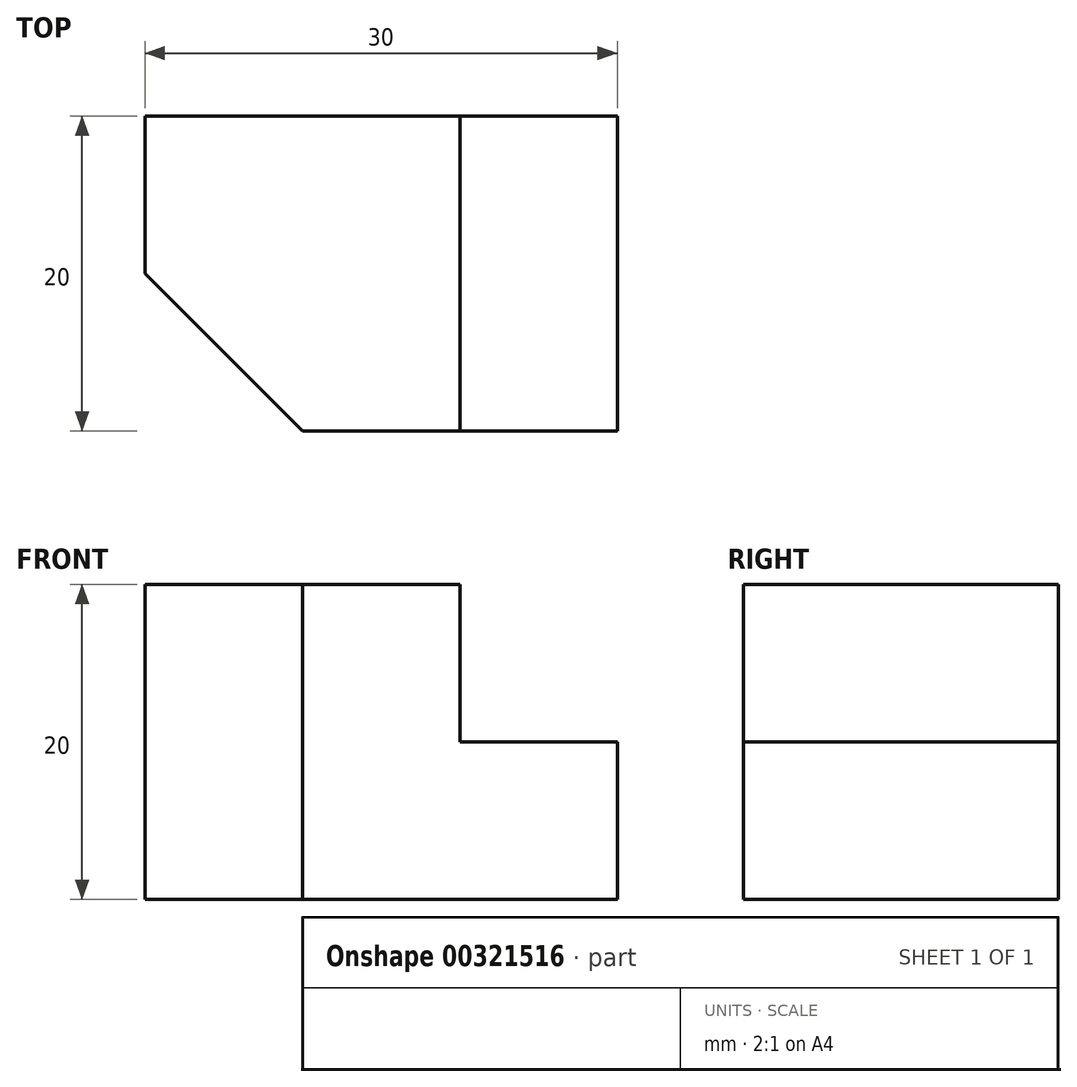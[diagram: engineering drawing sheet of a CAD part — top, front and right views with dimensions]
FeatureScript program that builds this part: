
annotation { "Feature Type Name" : "Feature", "Feature Type Description" : "" }
export const myFeature = defineFeature(function(context is Context, id is Id, definition is map)
    precondition{}
    {
        {
            var Q0;
            Q0=qCreatedBy(makeId("Front.planeOp"),FACE);
            var sketch = newSketch(context, id + "F0", { "sketchPlane" : qUnion([Q0])});
            skLineSegment(sketch, "E0.bottom", {"start": v(0, 0) * mm, "end": v(30, 0) * mm});
            skLineSegment(sketch, "E0.top", {"start": v(0, 20) * mm, "end": v(30, 20) * mm});
            skLineSegment(sketch, "E0.left", {"start": v(0, 0) * mm, "end": v(0, 20) * mm});
            skLineSegment(sketch, "E0.right", {"start": v(30, 0) * mm, "end": v(30, 20) * mm});
            skSolve(sketch);
        }
        {
            var Q0;
            Q0 = qSketchRegion(id + "F0", true);
            extrude(context, id + "F1", {"entities" : qUnion([Q0]), "depth" : (5 * 4) * mm});
        }
        {
            var Q0;
            Q0=makeQuery(id+"F1.opExtrude","CAP_FACE",FACE,{"disambiguationData":[OSD([sQuery(id+"F0.wireOp",EDGE,"E0.bottom"),sQuery(id+"F0.wireOp",EDGE,"E0.top"),sQuery(id+"F0.wireOp",EDGE,"E0.left"),sQuery(id+"F0.wireOp",EDGE,"E0.right")])],"isStart":false});
            var sketch = newSketch(context, id + "F2", { "sketchPlane" : qUnion([Q0])});
            skLineSegment(sketch, "E1.bottom", {"start": v(30, 20) * mm, "end": v(20, 20) * mm});
            skLineSegment(sketch, "E1.top", {"start": v(30, 10) * mm, "end": v(20, 10) * mm});
            skLineSegment(sketch, "E1.left", {"start": v(30, 20) * mm, "end": v(30, 10) * mm});
            skLineSegment(sketch, "E1.right", {"start": v(20, 20) * mm, "end": v(20, 10) * mm});
            skSolve(sketch);
        }
        {
            var Q0;
            Q0 = qSketchRegion(id + "F2", true);
            extrude(context, id + "F3", {"entities" : qUnion([Q0]), "operationType" : NewBodyOperationType.REMOVE, "endBound" : BoundingType.THROUGH_ALL, "oppositeDirection" : true, "depth" : 25 * mm});
        }
        {
            var Q0;
            Q0=makeQuery(id+"F1.opExtrude","SWEPT_FACE",FACE,{"disambiguationData":[OSD([sQuery(id+"F0.wireOp",EDGE,"E0.top")])]});
            var sketch = newSketch(context, id + "F4", { "sketchPlane" : qUnion([Q0])});
            skLineSegment(sketch, "E2", {"start": v(0, -20) * mm, "end": v(0, -10) * mm});
            skLineSegment(sketch, "E3", {"start": v(0, -20) * mm, "end": v(10, -20) * mm});
            skLineSegment(sketch, "E4", {"start": v(10, -20) * mm, "end": v(0, -10) * mm});
            skSolve(sketch);
        }
        {
            var Q0;
            Q0 = qSketchRegion(id + "F4", true);
            extrude(context, id + "F5", {"entities" : qUnion([Q0]), "operationType" : NewBodyOperationType.REMOVE, "endBound" : BoundingType.THROUGH_ALL, "oppositeDirection" : true, "depth" : 25 * mm});
        }
    });
